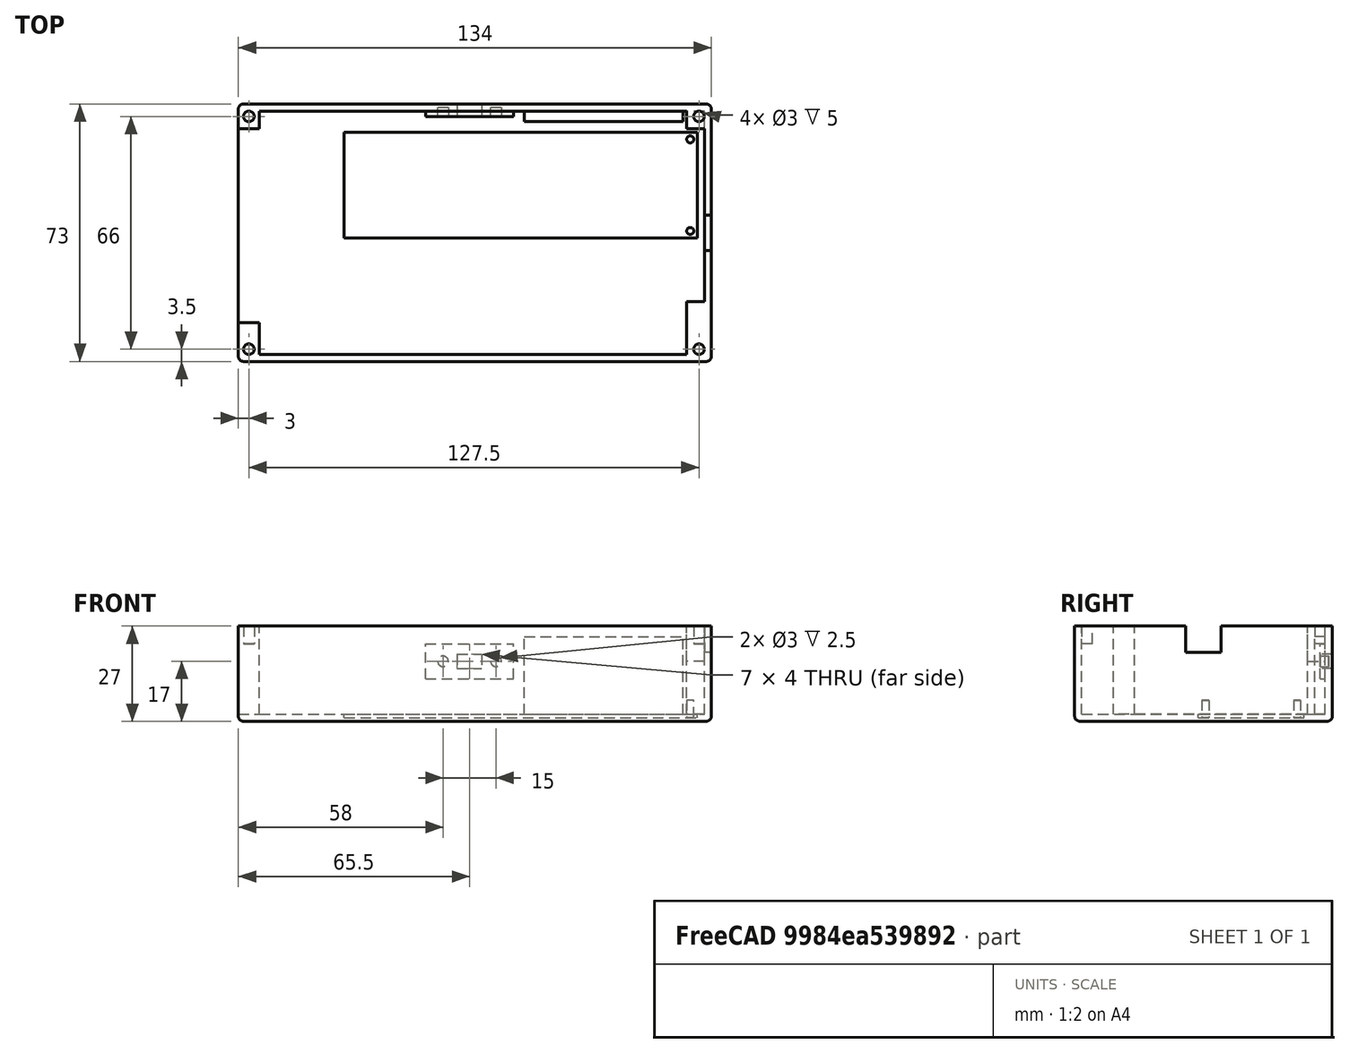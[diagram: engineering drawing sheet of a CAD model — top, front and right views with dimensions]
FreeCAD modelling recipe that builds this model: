
FCSTD DOCUMENT  (FreeCAD 1.0R39285 (Git))
Label: caseBottom
License: All rights reserved
LicenseURL: https://en.wikipedia.org/wiki/All_rights_reserved
objects: PartDesign::SubtractiveCylinder×6, PartDesign::AdditiveBox×5, PartDesign::SubtractiveBox×5, PartDesign::Fillet×4, PartDesign::AdditiveCylinder×2, PartDesign::Body×1
note: 67 computed .brp shape members not serialized (recipe doc carries the construction recipe); baked Part::Feature solids carry a one-line shape summary decoded from their .brp

FEATURE [PartDesign::AdditiveBox] Box  label="base"
  AttacherType = Attacher::AttachEngine3D
  Height = 27
  Length = 134
  Refine = true
  Suppressed = false
  Width = 73
FEATURE [PartDesign::SubtractiveBox] Box001  label="primaryHollow"
  AttacherType = Attacher::AttachEngine3D
  AttachmentOffset = pos=(6,2,-25) rot=(0,0,1;0rad)
  AttachmentSupport = -> [Box]
  BaseFeature = -> Box
  Height = 25
  Length = 126
  MapMode = 5
  Placement = pos=(6,2,2) rot=(0,0,1;0rad)
  Refine = true
  Suppressed = false
  Width = 69
FEATURE [PartDesign::SubtractiveBox] Box002  label="dacGap"
  AttacherType = Attacher::AttachEngine3D
  AttachmentOffset = pos=(-8,9,0) rot=(0,0,1;0rad)
  AttachmentSupport = -> [Box001]
  BaseFeature = -> Box001
  Height = 25
  Length = 10
  MapMode = 5
  Placement = pos=(-2,11,2) rot=(0,0,1;0rad)
  Refine = true
  Suppressed = false
  Width = 55
FEATURE [PartDesign::SubtractiveBox] Box003  label="batteryPCBRecess"
  AttacherType = Attacher::AttachEngine3D
  AttachmentOffset = pos=(32,24,-1) rot=(0,0,1;0rad)
  AttachmentSupport = -> [Box002]
  BaseFeature = -> Box002
  Height = 1
  Length = 100
  MapMode = 5
  Placement = pos=(30,35,1) rot=(0,0,1;0rad)
  Refine = true
  Suppressed = false
  Width = 30
FEATURE [PartDesign::AdditiveCylinder] Cylinder  label="batteryPCBRecessSupport1"
  Angle = 360
  AttacherType = Attacher::AttachEngine3D
  AttachmentOffset = pos=(98,2,0) rot=(0,0,1;0rad)
  AttachmentSupport = -> [Box003]
  BaseFeature = -> Box003
  FirstAngle = 0
  Height = 5
  MapMode = 5
  Placement = pos=(128,37,1) rot=(0,0,1;0rad)
  Radius = 1
  Refine = true
  SecondAngle = 0
  Suppressed = false
FEATURE [PartDesign::AdditiveCylinder] Cylinder001  label="batteryPCBRecessSupport2"
  Angle = 360
  AttacherType = Attacher::AttachEngine3D
  AttachmentOffset = pos=(0,26,0) rot=(0,0,1;0rad)
  AttachmentSupport = -> [Cylinder]
  BaseFeature = -> Cylinder
  FirstAngle = 0
  Height = 5
  MapMode = 5
  Placement = pos=(128,63,1) rot=(0,0,1;0rad)
  Radius = 1
  Refine = true
  SecondAngle = 0
  Suppressed = false
FEATURE [PartDesign::AdditiveBox] Box004  label="powerSwitchBase"
  AttacherType = Attacher::AttachEngine3D
  AttachmentOffset = pos=(-75,6.5,10) rot=(0,0,1;0rad)
  AttachmentSupport = -> [Cylinder001]
  BaseFeature = -> Cylinder001
  Height = 10
  Length = 25
  MapMode = 5
  Placement = pos=(53,69.5,12) rot=(0,0,1;0rad)
  Refine = true
  Suppressed = false
  Width = 1.5
FEATURE [PartDesign::SubtractiveBox] Box005  label="powerSwitchCutout"
  AttacherType = Attacher::AttachEngine3D
  AttachmentOffset = pos=(9,3,-5) rot=(0,0,1;0rad)
  AttachmentSupport = -> [Box004]
  BaseFeature = -> Box004
  Height = 7
  Length = 7
  MapMode = 5
  Placement = pos=(62,74.5,15) rot=(1,0,0;1.5708rad)
  Refine = true
  Suppressed = false
  Width = 4
FEATURE [PartDesign::SubtractiveCylinder] Cylinder002  label="powerSwitchHeatInsert1"
  Angle = 360
  AttacherType = Attacher::AttachEngine3D
  AttachmentOffset = pos=(-4,2,-2.5) rot=(0,0,1;0rad)
  AttachmentSupport = -> [Box005]
  BaseFeature = -> Box005
  FirstAngle = 0
  Height = 2.5
  MapMode = 5
  Placement = pos=(58,72,17) rot=(1,0,0;1.5708rad)
  Radius = 1.5
  Refine = true
  SecondAngle = 0
  Suppressed = false
FEATURE [PartDesign::SubtractiveCylinder] Cylinder003  label="powerSwitchHeatInsert2"
  Angle = 360
  AttacherType = Attacher::AttachEngine3D
  AttachmentOffset = pos=(15,0,-2.5) rot=(0,0,1;0rad)
  AttachmentSupport = -> [Cylinder002]
  BaseFeature = -> Cylinder002
  FirstAngle = 0
  Height = 2.5
  MapMode = 5
  Placement = pos=(73,72,17) rot=(1,0,0;1.5708rad)
  Radius = 1.5
  Refine = true
  SecondAngle = 0
  Suppressed = false
FEATURE [PartDesign::AdditiveBox] Box006  label="clickwheelSupport"
  AttacherType = Attacher::AttachEngine3D
  AttachmentOffset = pos=(8,-15,0) rot=(0,0,1;0rad)
  AttachmentSupport = -> [Cylinder003]
  BaseFeature = -> Cylinder003
  Height = 3
  Length = 45
  MapMode = 5
  Placement = pos=(81,71,2) rot=(1,0,0;1.5708rad)
  Refine = true
  Suppressed = false
  Width = 22
FEATURE [PartDesign::SubtractiveBox] Box007  label="chargingPort"
  AttacherType = Attacher::AttachEngine3D
  AttachmentOffset = pos=(-25,29.5,-2) rot=(0,0,1;0rad)
  AttachmentSupport = -> [Box006]
  BaseFeature = -> Box006
  Height = 2
  Length = 7.5
  MapMode = 5
  Placement = pos=(134,41.5,27) rot=(0.707107,0,-0.707107;3.14159rad)
  Refine = true
  Suppressed = false
  Width = 10
FEATURE [PartDesign::AdditiveBox] Box008  label="bottomLeftScrewSupport"
  AttacherType = Attacher::AttachEngine3D
  AttachmentOffset = pos=(-39.5,2,0) rot=(0,0,1;0rad)
  AttachmentSupport = -> [Box007]
  BaseFeature = -> Box007
  Height = 25
  Length = 15
  MapMode = 5
  Placement = pos=(132,2,2) rot=(0,0,1;1.5708rad)
  Refine = true
  Suppressed = false
  Width = 5
FEATURE [PartDesign::AdditiveBox] Box009  label="bottomRightScrewSupport"
  AttacherType = Attacher::AttachEngine3D
  AttachmentOffset = pos=(64,0,15) rot=(0,0,1;0rad)
  AttachmentSupport = -> [Box008]
  BaseFeature = -> Box008
  Height = 10
  Length = 5
  MapMode = 5
  Placement = pos=(132,66,17) rot=(0,0,1;1.5708rad)
  Refine = true
  Suppressed = false
  Width = 5
FEATURE [PartDesign::SubtractiveCylinder] Cylinder004  label="bottomRightScrew"
  Angle = 360
  AttacherType = Attacher::AttachEngine3D
  AttachmentOffset = pos=(3.5,1.5,-5) rot=(0,0,1;0rad)
  AttachmentSupport = -> [Box009]
  BaseFeature = -> Box009
  FirstAngle = 0
  Height = 5
  MapMode = 5
  Placement = pos=(130.5,69.5,22) rot=(0,0,1;1.5708rad)
  Radius = 1.5
  Refine = true
  SecondAngle = 0
  Suppressed = false
FEATURE [PartDesign::SubtractiveCylinder] Cylinder005  label="bottomLeftScrew"
  Angle = 360
  AttacherType = Attacher::AttachEngine3D
  AttachmentOffset = pos=(-66,0,-5) rot=(0,0,1;0rad)
  AttachmentSupport = -> [Cylinder004]
  BaseFeature = -> Cylinder004
  FirstAngle = 0
  Height = 5
  MapMode = 5
  Placement = pos=(130.5,3.5,22) rot=(0,0,1;1.5708rad)
  Radius = 1.5
  Refine = true
  SecondAngle = 0
  Suppressed = false
FEATURE [PartDesign::SubtractiveCylinder] Cylinder006  label="topLeftScrew"
  Angle = 360
  AttacherType = Attacher::AttachEngine3D
  AttachmentOffset = pos=(0,127.5,-5) rot=(0,0,1;0rad)
  AttachmentSupport = -> [Cylinder005]
  BaseFeature = -> Cylinder005
  FirstAngle = 0
  Height = 5
  MapMode = 5
  Placement = pos=(3,3.5,22) rot=(0,0,1;1.5708rad)
  Radius = 1.5
  Refine = true
  SecondAngle = 0
  Suppressed = false
FEATURE [PartDesign::SubtractiveCylinder] Cylinder007  label="topRightScrew"
  Angle = 360
  AttacherType = Attacher::AttachEngine3D
  AttachmentOffset = pos=(66,0,-5) rot=(0,0,1;0rad)
  AttachmentSupport = -> [Cylinder006]
  BaseFeature = -> Cylinder006
  FirstAngle = 0
  Height = 5
  MapMode = 5
  Placement = pos=(3,69.5,22) rot=(0,0,1;1.5708rad)
  Radius = 1.5
  Refine = true
  SecondAngle = 0
  Suppressed = false
FEATURE [PartDesign::Fillet] Fillet
  Base = -> Cylinder007 [Edge58]
  BaseFeature = -> Cylinder007
  Placement = pos=(3,69.5,22) rot=(0,0,1;1.5708rad)
  Radius = 1.5
  Refine = true
  SupportTransform = false
  Suppressed = false
  UseAllEdges = false
FEATURE [PartDesign::Fillet] Fillet001
  Base = -> Fillet [Edge28]
  BaseFeature = -> Fillet
  Placement = pos=(3,69.5,22) rot=(0,0,1;1.5708rad)
  Radius = 1.5
  Refine = true
  SupportTransform = false
  Suppressed = false
  UseAllEdges = false
FEATURE [PartDesign::Fillet] Fillet002
  Base = -> Fillet001 [Edge1]
  BaseFeature = -> Fillet001
  Placement = pos=(3,69.5,22) rot=(0,0,1;1.5708rad)
  Radius = 1.5
  Refine = true
  SupportTransform = false
  Suppressed = false
  UseAllEdges = false
FEATURE [PartDesign::Fillet] Fillet003
  Base = -> Fillet002 [Edge48,Edge55,Edge67]
  BaseFeature = -> Fillet002
  Placement = pos=(3,69.5,22) rot=(0,0,1;1.5708rad)
  Radius = 1.5
  Refine = true
  SupportTransform = false
  Suppressed = false
  UseAllEdges = false
FEATURE [PartDesign::Body] Body
  AllowCompound = false
  Group = -> [Box,Box001,Box002,Box003,Cylinder,Cylinder001,Box004,Box005,Cylinder002,Cylinder003,Box006,Box007,Box008,Box009,Cylinder004,Cylinder005,Cylinder006,Cylinder007,Fillet,Fillet001,Fillet002,Fillet003]
  Origin = -> Origin
  Tip = -> Fillet003
